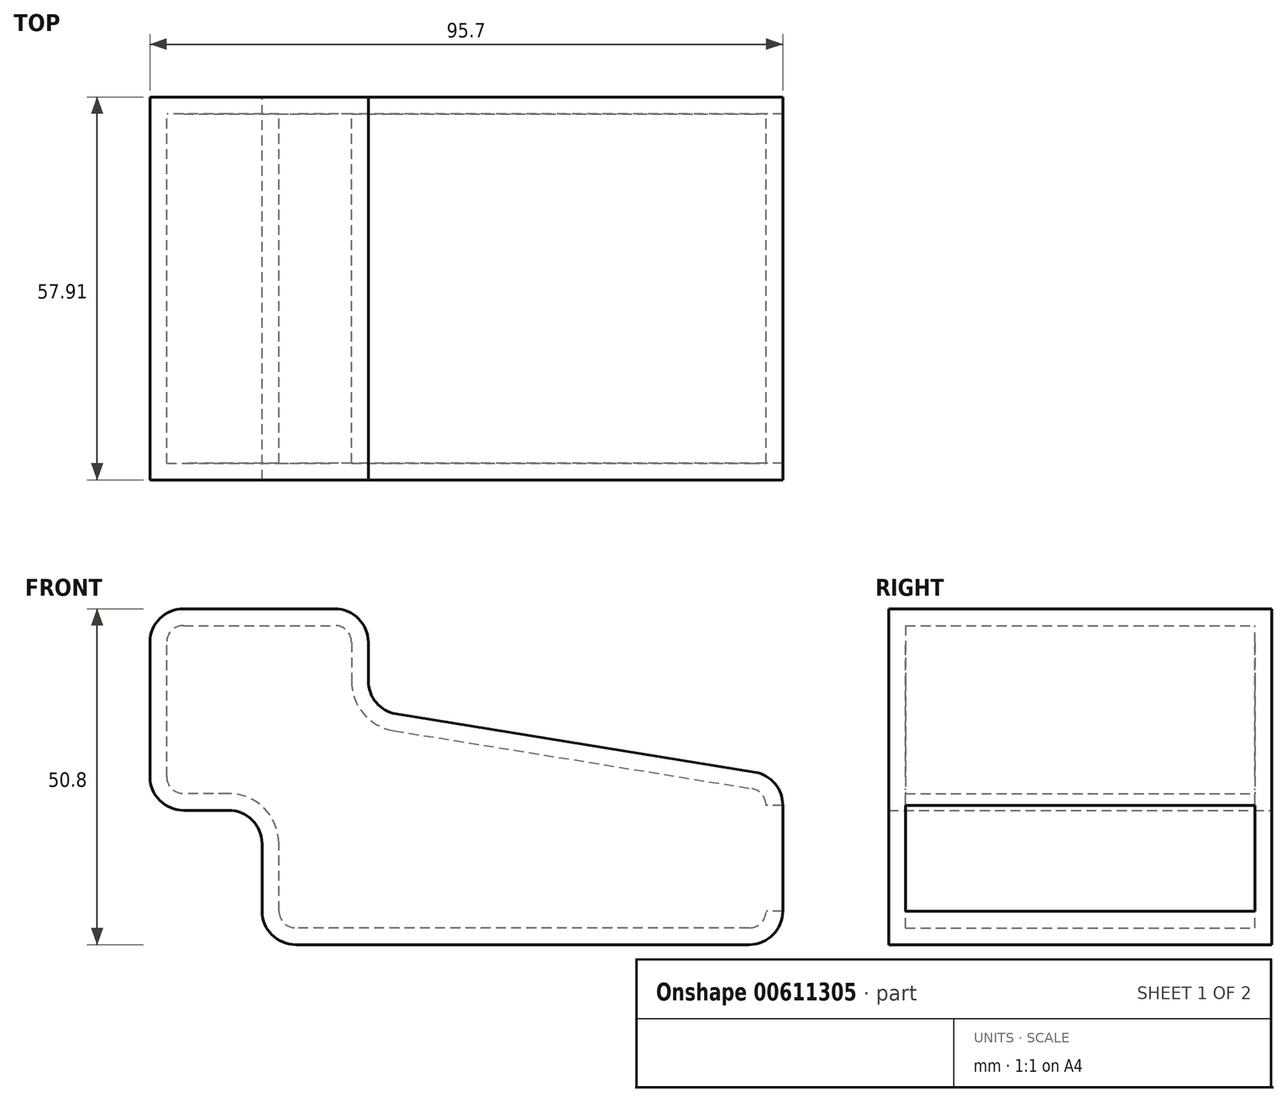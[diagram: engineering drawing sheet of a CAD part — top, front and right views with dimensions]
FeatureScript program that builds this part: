
annotation { "Feature Type Name" : "Feature", "Feature Type Description" : "" }
export const myFeature = defineFeature(function(context is Context, id is Id, definition is map)
    precondition{}
    {
        {
            var Q0;
            Q0=qCreatedBy(makeId("Front.planeOp"),FACE);
            var sketch = newSketch(context, id + "F0", { "sketchPlane" : qUnion([Q0])});
            skLineSegment(sketch, "E0", {"start": v(-40.25, 44.16) * mm, "end": v(-7.23, 44.16) * mm});
            skLineSegment(sketch, "E1", {"start": v(-7.23, 44.16) * mm, "end": v(-7.23, 28.92) * mm});
            skLineSegment(sketch, "E2", {"start": v(-7.23, 28.92) * mm, "end": v(55.45, 18.76) * mm});
            skLineSegment(sketch, "E3", {"start": v(55.45, 18.76) * mm, "end": v(55.45, -6.64) * mm});
            skLineSegment(sketch, "E4", {"start": v(55.45, -6.64) * mm, "end": v(-23.3, -6.64) * mm});
            skLineSegment(sketch, "E5", {"start": v(-23.3, -6.64) * mm, "end": v(-23.3, 13.68) * mm});
            skLineSegment(sketch, "E6", {"start": v(-23.3, 13.68) * mm, "end": v(-40.25, 13.68) * mm});
            skLineSegment(sketch, "E7", {"start": v(-40.25, 13.68) * mm, "end": v(-40.25, 44.16) * mm});
            skSolve(sketch);
        }
        {
            var Q0;
            Q0=makeQuery(id+"F0.imprint","IMPRINT",FACE,{"disambiguationData":[TD([[makeQuery(id+"F0.imprint","IMPRINT",EDGE,{"derivedFrom":sQuery(id+"F0.wireOp",EDGE,"E0")}),-1.0]])]});
            extrude(context, id + "F1", {"entities" : qUnion([Q0]), "depth" : 57.9 * mm, "offsetDistance" : 25.4 * mm});
        }
        {
            var Q0;
            Q0=makeQuery(id+"F1.opExtrude","SWEPT_EDGE",EDGE,{"disambiguationData":[OSD([sQuery(id+"F0.wireOp",EDGE,"E0"),sQuery(id+"F0.wireOp",EDGE,"E1")])]});
            var Q1;
            Q1=makeQuery(id+"F1.opExtrude","SWEPT_EDGE",EDGE,{"disambiguationData":[OSD([sQuery(id+"F0.wireOp",EDGE,"E1"),sQuery(id+"F0.wireOp",EDGE,"E2")])]});
            var Q2;
            Q2=makeQuery(id+"F1.opExtrude","SWEPT_EDGE",EDGE,{"disambiguationData":[OSD([sQuery(id+"F0.wireOp",EDGE,"E2"),sQuery(id+"F0.wireOp",EDGE,"E3")])]});
            var Q3;
            Q3=makeQuery(id+"F1.opExtrude","SWEPT_EDGE",EDGE,{"disambiguationData":[OSD([sQuery(id+"F0.wireOp",EDGE,"E3"),sQuery(id+"F0.wireOp",EDGE,"E4")])]});
            var Q4;
            Q4=makeQuery(id+"F1.opExtrude","SWEPT_EDGE",EDGE,{"disambiguationData":[OSD([sQuery(id+"F0.wireOp",EDGE,"E0"),sQuery(id+"F0.wireOp",EDGE,"E7")])]});
            var Q5;
            Q5=makeQuery(id+"F1.opExtrude","SWEPT_EDGE",EDGE,{"disambiguationData":[OSD([sQuery(id+"F0.wireOp",EDGE,"E6"),sQuery(id+"F0.wireOp",EDGE,"E7")])]});
            var Q6;
            Q6=makeQuery(id+"F1.opExtrude","SWEPT_EDGE",EDGE,{"disambiguationData":[OSD([sQuery(id+"F0.wireOp",EDGE,"E5"),sQuery(id+"F0.wireOp",EDGE,"E6")])]});
            var Q7;
            Q7=makeQuery(id+"F1.opExtrude","SWEPT_EDGE",EDGE,{"disambiguationData":[OSD([sQuery(id+"F0.wireOp",EDGE,"E4"),sQuery(id+"F0.wireOp",EDGE,"E5")])]});
            fillet(context, id + "F2", {"entities" : qUnion([Q0, Q1, Q2, Q3, Q4, Q5, Q6, Q7]), "radius" : 5.08 * mm, "tangentPropagation" : true, "allowEdgeOverflow" : false});
        }
        {
            var Q0;
            Q0=makeQuery(id+"F1.opExtrude","SWEPT_FACE",FACE,{"disambiguationData":[OSD([sQuery(id+"F0.wireOp",EDGE,"E3")])]});
            shell(context, id + "F3", {"entities" : qUnion([Q0]), "thickness" : 2.54 * mm});
        }
    });
